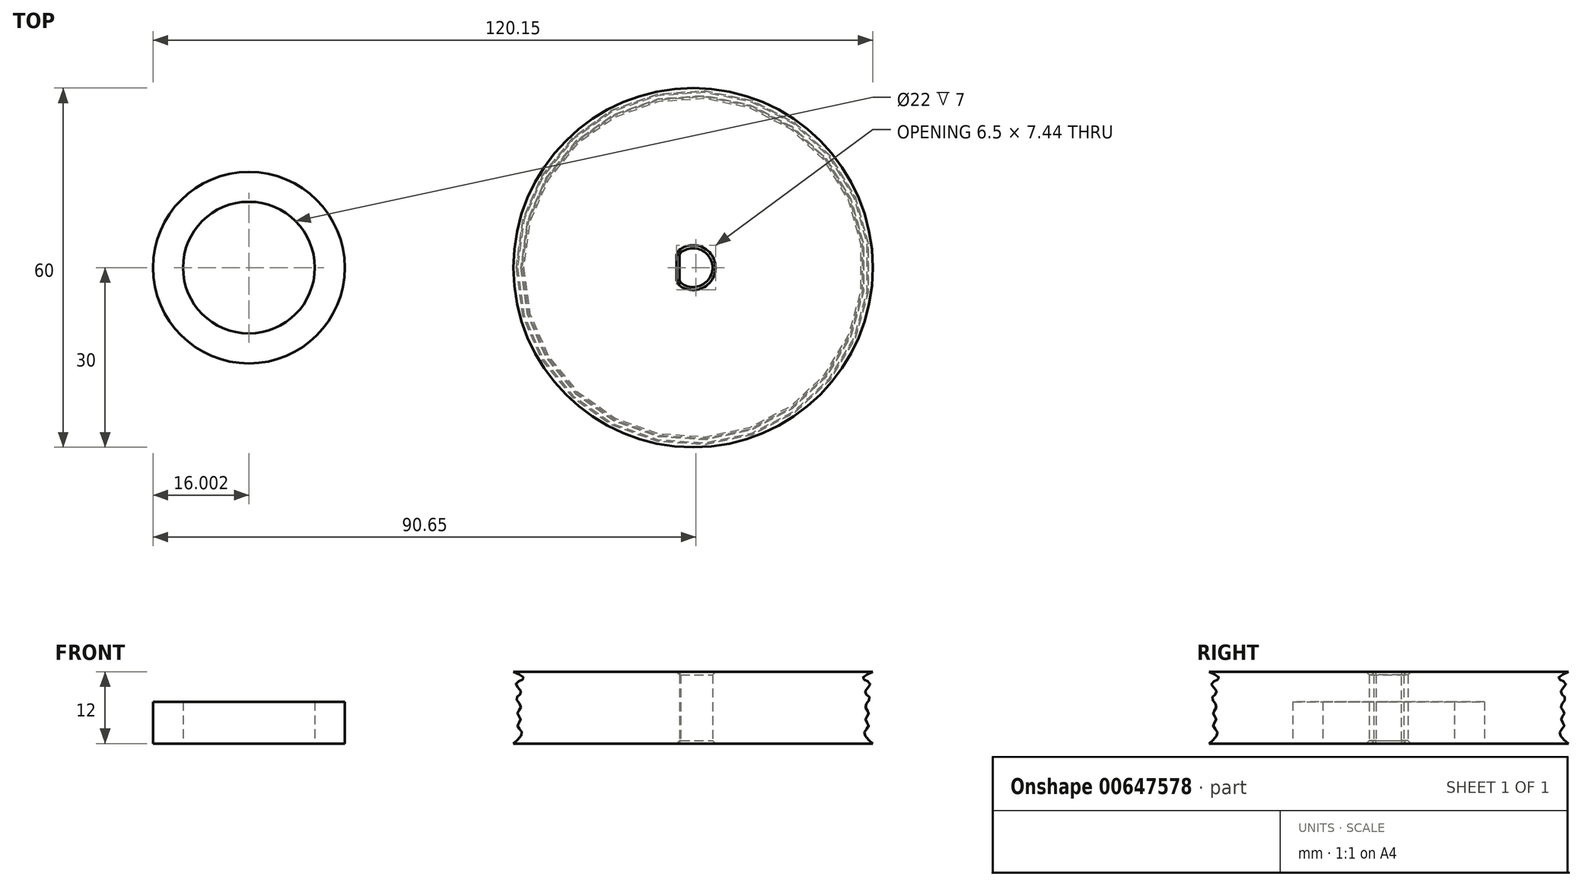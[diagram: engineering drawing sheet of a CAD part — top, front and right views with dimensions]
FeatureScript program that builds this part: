
annotation { "Feature Type Name" : "Feature", "Feature Type Description" : "" }
export const myFeature = defineFeature(function(context is Context, id is Id, definition is map)
    precondition{}
    {
        {
            var Q0;
            Q0=qCreatedBy(makeId("Top.planeOp"),FACE);
            var sketch = newSketch(context, id + "F0", { "sketchPlane" : qUnion([Q0])});
            skCircle(sketch, "E0", {"center": v(0, 0) * mm, "radius": 30 * mm});
            skArc(sketch, "E1", {"start": v(-2.25, -2.35) * mm, "mid": v(3.25, 0) * mm, "end": v(-2.25, 2.35) * mm});
            skLineSegment(sketch, "E2", {"start": v(-2.25, 2.35) * mm, "end": v(-2.25, -2.35) * mm});
            skSolve(sketch);
        }
        {
            var Q0;
            Q0=makeQuery(id+"F0.imprint","IMPRINT",FACE,{"disambiguationData":[TD([[makeQuery(id+"F0.imprint","IMPRINT",EDGE,{"derivedFrom":sQuery(id+"F0.wireOp",EDGE,"E0")}),1.0]])]});
            extrude(context, id + "F1", {"entities" : qUnion([Q0]), "depth" : 12 * mm, "offsetDistance" : 25 * mm});
        }
        {
            var Q0;
            Q0=qCreatedBy(makeId("Top.planeOp"),FACE);
            var sketch = newSketch(context, id + "F2", { "sketchPlane" : qUnion([Q0])});
            skCircle(sketch, "E3", {"center": v(-74.15, 0) * mm, "radius": 11 * mm});
            skCircle(sketch, "E4.0", {"center": v(-74.15, 0) * mm, "radius": 16 * mm});
            skSolve(sketch);
        }
        {
            var Q0;
            Q0=makeQuery(id+"F2.imprint","IMPRINT",FACE,{"disambiguationData":[TD([[makeQuery(id+"F2.imprint","IMPRINT",EDGE,{"derivedFrom":sQuery(id+"F2.wireOp",EDGE,"E3")}),-1.0]])]});
            extrude(context, id + "F3", {"entities" : qUnion([Q0]), "depth" : 7 * mm, "offsetDistance" : 25 * mm});
        }
        {
            var Q0;
            Q0=qCreatedBy(makeId("Front.planeOp"),FACE);
            var sketch = newSketch(context, id + "F4", { "sketchPlane" : qUnion([Q0])});
            skLineSegment(sketch, "E5", {"start": v(30, 12) * mm, "end": v(30, 0) * mm});
            skFitSpline(sketch, "E6", {"points": [v(30, 12) * mm, v(28.33, 10.8) * mm, v(29.58, 10) * mm, v(28.69, 8.55) * mm, v(29.49, 7.58) * mm, v(28.73, 6.19) * mm, v(29.32, 5.1) * mm, v(28.79, 4.05) * mm, v(29.33, 3) * mm, v(28.57, 1.9) * mm, v(30, 0) * mm], "startDerivative": vector(-24.16, -11.37) * mm, "endDerivative": vector(18.86, -16.2) * mm});
            skSolve(sketch);
        }
        {
            var Q0;
            Q0=qCreatedBy(makeId("Front.planeOp"),FACE);
            var sketch = newSketch(context, id + "F5", { "sketchPlane" : qUnion([Q0])});
            skLineSegment(sketch, "E7", {"start": v(0, 11.94) * mm, "end": v(0, 0) * mm});
            skSolve(sketch);
        }
        {
            var Q0;
            Q0 = qSketchRegion(id + "F4", true);
            var Q1;
            Q1=sQuery(id+"F5.wireOp",EDGE,"E7");
            revolve(context, id + "F6", {"operationType" : NewBodyOperationType.REMOVE, "surfaceOperationType" : NewSurfaceOperationType.NEW, "entities" : qUnion([Q0]), "axis" : qUnion([Q1]), "revolveType" : RevolveType.FULL, "oppositeDirection" : true});
        }
        {
            var Q0;
            Q0=makeQuery(id+"F1.opExtrude","SWEPT_FACE",FACE,{"disambiguationData":[OSD([sQuery(id+"F0.wireOp",EDGE,"E1")])]});
            var Q1;
            Q1=makeQuery(id+"F1.opExtrude","SWEPT_FACE",FACE,{"disambiguationData":[OSD([sQuery(id+"F0.wireOp",EDGE,"E2")])]});
            chamfer(context, id + "F7", {"entities" : qUnion([Q0, Q1]), "width" : .5 * mm, "tangentPropagation" : true});
        }
    });
